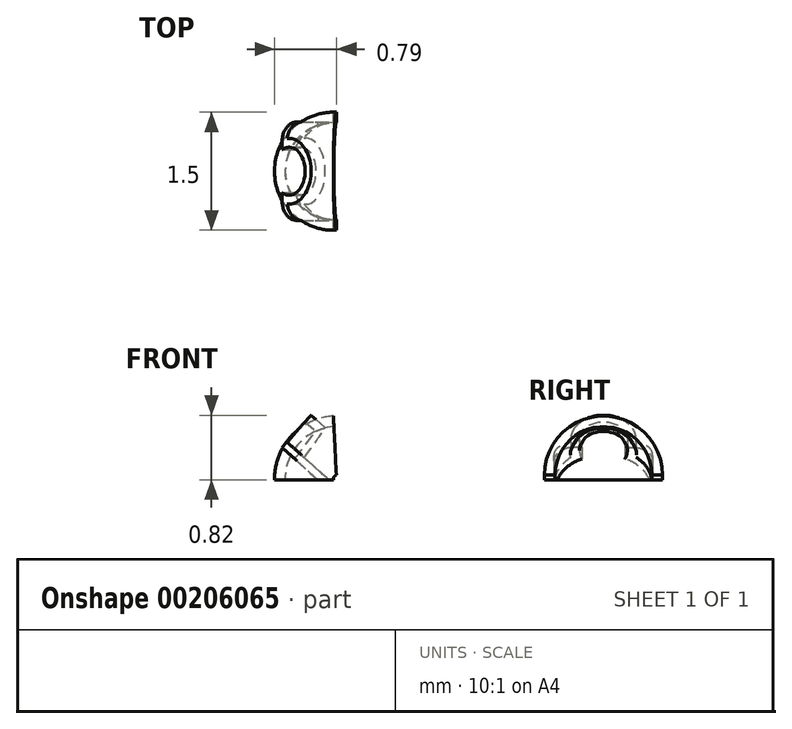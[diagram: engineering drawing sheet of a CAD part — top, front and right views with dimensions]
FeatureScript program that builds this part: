
annotation { "Feature Type Name" : "Feature", "Feature Type Description" : "" }
export const myFeature = defineFeature(function(context is Context, id is Id, definition is map)
    precondition{}
    {
        {
            var Q0;
            Q0=qCreatedBy(makeId("Top.planeOp"),FACE);
            var sketch = newSketch(context, id + "F0", { "sketchPlane" : qUnion([Q0])});
            skLineSegment(sketch, "E0", {"start": v(0, -0.75) * mm, "end": v(0, -0.62) * mm});
            skArc(sketch, "E1", {"start": v(0, 0.75) * mm, "mid": v(-0.75, 0) * mm, "end": v(0, -0.75) * mm});
            skArc(sketch, "E2.0", {"start": v(0, 0.62) * mm, "mid": v(-0.62, 0) * mm, "end": v(0, -0.62) * mm});
            skLineSegment(sketch, "E3.trimOffspring", {"start": v(0, 0.62) * mm, "end": v(0, 0.75) * mm});
            skSolve(sketch);
        }
        {
            var Q0;
            Q0=qCreatedBy(makeId("Front.planeOp"),FACE);
            var sketch = newSketch(context, id + "F1", { "sketchPlane" : qUnion([Q0])});
            skArc(sketch, "E4", {"start": v(0, 0.76) * mm, "mid": v(-0.5, 0.52) * mm, "end": v(-0.7, 0) * mm});
            skSolve(sketch);
        }
        {
            var Q0;
            Q0 = qSketchRegion(id + "F0", true);
            var Q1;
            Q1=qConstructionFilter(qBodyType(qCreatedBy(id+"F0",EDGE),BodyType.WIRE),ConstructionObject.NO);
            var Q2;
            Q2=qConstructionFilter(qBodyType(qCreatedBy(id+"F1",EDGE),BodyType.WIRE),ConstructionObject.NO);
            sweep(context, id + "F2", {"profiles" : qUnion([Q0]), "surfaceProfiles" : qUnion([Q1]), "path" : qUnion([Q2])});
        }
        {
            var Q0;
            Q0=makeQuery(id+"F2.opSweep","CAP_FACE",FACE,{"disambiguationData":[OSD([sQuery(id+"F0.wireOp",EDGE,"E0"),sQuery(id+"F0.wireOp",EDGE,"E1"),sQuery(id+"F0.wireOp",EDGE,"E2.0"),sQuery(id+"F0.wireOp",EDGE,"E3.trimOffspring"),sQuery(id+"F1.wireOp",VERTEX,"E4.start")])],"isStart":false});
            var Q1;
            Q1=sQuery(id+"F0.wireOp",EDGE,"E0");
            cPlane(context, id + "F3", {"entities" : qUnion([Q0, Q1]), "cplaneType" : CPlaneType.LINE_ANGLE, "offset" : 25.4 * mm, "angle" : 45 * degree, "width" : 152.4 * mm, "height" : 152.4 * mm});
        }
        {
            var Q0;
            Q0=qCreatedBy(id+"F3.planeOp",FACE);
            var sketch = newSketch(context, id + "F4", { "sketchPlane" : qUnion([Q0])});
            skArc(sketch, "E5", {"start": v(0.27, -0.13) * mm, "mid": v(0, 0.3) * mm, "end": v(-0.27, -0.13) * mm});
            skArc(sketch, "E6", {"start": v(0.41, -0.04) * mm, "mid": v(0, 0.42) * mm, "end": v(-0.41, -0.04) * mm});
            skLineSegment(sketch, "E7", {"start": v(0.27, -0.13) * mm, "end": v(0.63, -0.13) * mm});
            skLineSegment(sketch, "E8", {"start": v(0.63, -0.13) * mm, "end": v(0.63, -0.04) * mm});
            skLineSegment(sketch, "E9", {"start": v(0.63, -0.04) * mm, "end": v(0.41, -0.04) * mm});
            skLineSegment(sketch, "E10", {"start": v(0, 0) * mm, "end": v(0, -0.13) * mm});
            skLineSegment(sketch, "E11.MirrorCS", {"start": v(-0.63, -0.13) * mm, "end": v(-0.63, -0.04) * mm});
            skLineSegment(sketch, "E12.MirrorCS", {"start": v(-0.27, -0.13) * mm, "end": v(-0.63, -0.13) * mm});
            skLineSegment(sketch, "E13.MirrorCS", {"start": v(-0.63, -0.04) * mm, "end": v(-0.41, -0.04) * mm});
            skSolve(sketch);
        }
        {
            var Q0;
            Q0 = qSketchRegion(id + "F4", true);
            extrude(context, id + "F5", {"entities" : qUnion([Q0]), "depth" : 0.76 * mm});
        }
        {
            var Q0;
            Q0=makeQuery(id+"F5.opExtrude","CAP_FACE",FACE,{"disambiguationData":[OSD([sQuery(id+"F4.wireOp",EDGE,"E5"),sQuery(id+"F4.wireOp",EDGE,"E6"),sQuery(id+"F4.wireOp",EDGE,"E7"),sQuery(id+"F4.wireOp",EDGE,"E8"),sQuery(id+"F4.wireOp",EDGE,"E9"),sQuery(id+"F4.wireOp",EDGE,"E11.MirrorCS"),sQuery(id+"F4.wireOp",EDGE,"E12.MirrorCS"),sQuery(id+"F4.wireOp",EDGE,"E13.MirrorCS")])],"isStart":true});
            var Q1;
            {var subQ0=sQuery(id+"F0.wireOp",EDGE,"E2.0");Q1=makeQuery(id+"F5.boolean.opBoolean","SPLIT",FACE,{"disambiguationData":[TD([makeQuery(id+"F5.opExtrude","SWEPT_FACE",FACE,{"disambiguationData":[OSD([sQuery(id+"F4.wireOp",EDGE,"E5")])]})])],"derivedFrom":makeQuery(id+"F2.opSweep","SWEPT_FACE",FACE,{"disambiguationData":[OSD([subQ0,sQuery(id+"F1.wireOp",EDGE,"E4")])]})});}
            var Q2;
            Q2=makeQuery(id+"F2.opSweep","SWEPT_BODY",BODY,{"disambiguationData":[OSD([sQuery(id+"F0.wireOp",EDGE,"E0"),sQuery(id+"F0.wireOp",EDGE,"E1"),sQuery(id+"F0.wireOp",EDGE,"E2.0"),sQuery(id+"F0.wireOp",EDGE,"E3.trimOffspring"),sQuery(id+"F1.wireOp",EDGE,"E4")])]});
            extrude(context, id + "F6", {"entities" : qUnion([Q0]), "operationType" : NewBodyOperationType.REMOVE, "endBound" : BoundingType.UP_TO_BODY, "oppositeDirection" : true, "endBoundEntityFace" : qUnion([Q1]), "endBoundEntityBody" : qUnion([Q2]), "depth" : 0.38 * mm});
        }
        {
            var Q0;
            Q0=makeQuery(id+"F5.opExtrude","CAP_EDGE",EDGE,{"disambiguationData":[OSD([sQuery(id+"F4.wireOp",EDGE,"E11.MirrorCS")])],"isStart":false});
            var Q1;
            Q1=makeQuery(id+"F5.opExtrude","CAP_EDGE",EDGE,{"disambiguationData":[OSD([sQuery(id+"F4.wireOp",EDGE,"E8")])],"isStart":false});
            fillet(context, id + "F7", {"entities" : qUnion([Q0, Q1]), "radius" : 0.25 * mm, "tangentPropagation" : true, "allowEdgeOverflow" : false});
        }
    });
